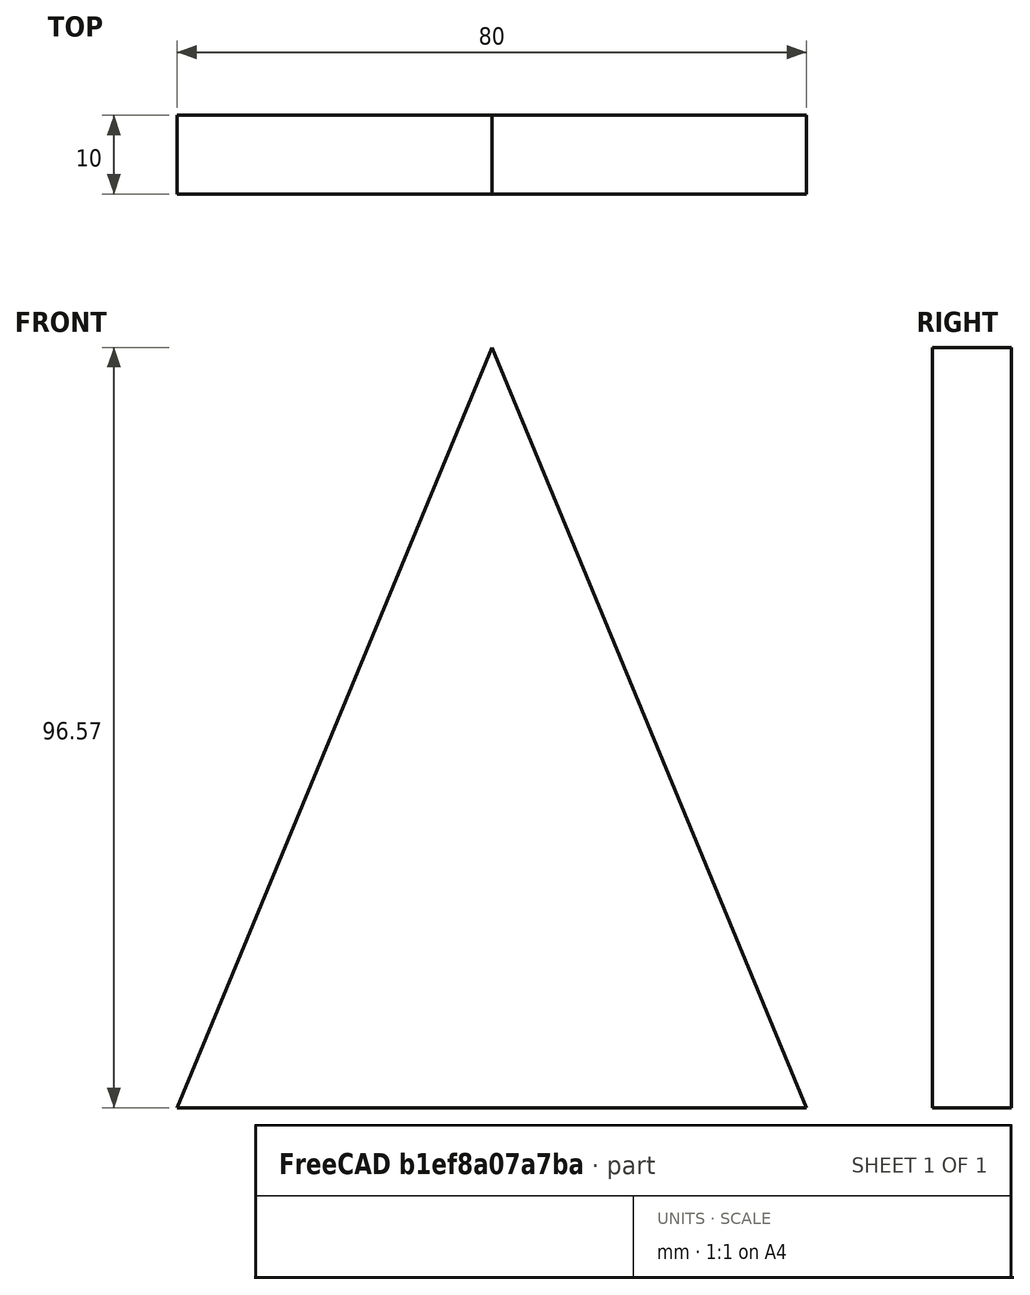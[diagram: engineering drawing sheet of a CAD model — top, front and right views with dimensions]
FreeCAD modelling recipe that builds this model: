
FCSTD DOCUMENT  (FreeCAD 0.20R29177 +233 (Git))
Label: triangulo
License: Creative Commons Attribution-ShareAlike
LicenseURL: http://creativecommons.org/licenses/by-sa/4.0/
objects: Sketcher::SketchObject×1, Part::Extrusion×1
note: 2 computed .brp shape members not serialized (recipe doc carries the construction recipe); baked Part::Feature solids carry a one-line shape summary decoded from their .brp

FEATURE [Sketcher::SketchObject] Sketch
  FullyConstrained = true
  Placement = pos=(0,0,0) rot=(1,0,0;1.5708rad)
  sketch-geometry (3):
    g0: LineSegment StartX=-40 StartY=0 StartZ=0 EndX=0 EndY=96.5685 EndZ=0
    g1: LineSegment StartX=0 StartY=96.5685 StartZ=0 EndX=40 EndY=0 EndZ=0
    g2: LineSegment StartX=40 StartY=0 StartZ=0 EndX=-40 EndY=0 EndZ=0
  constraints (8):
    c: Coincident(g0,g1)
    c: Coincident(g1,g2)
    c: Coincident(g2,g0)
    c: PointOnObject(g1,g-1)
    c: PointOnObject(g0,g-2)
    c: Angle(g0,g1) = 0.785398
    c: DistanceX(g2,g2) = 80
    c: Symmetric(g1,g0,g-2)
FEATURE [Part::Extrusion] Extrude
  Base = -> Sketch
  Dir = (0,-1,0)
  DirMode = 0
  FaceMakerClass = Part::FaceMakerBullseye
  LengthFwd = 10
  LengthRev = 0
  Solid = true
  Symmetric = false
